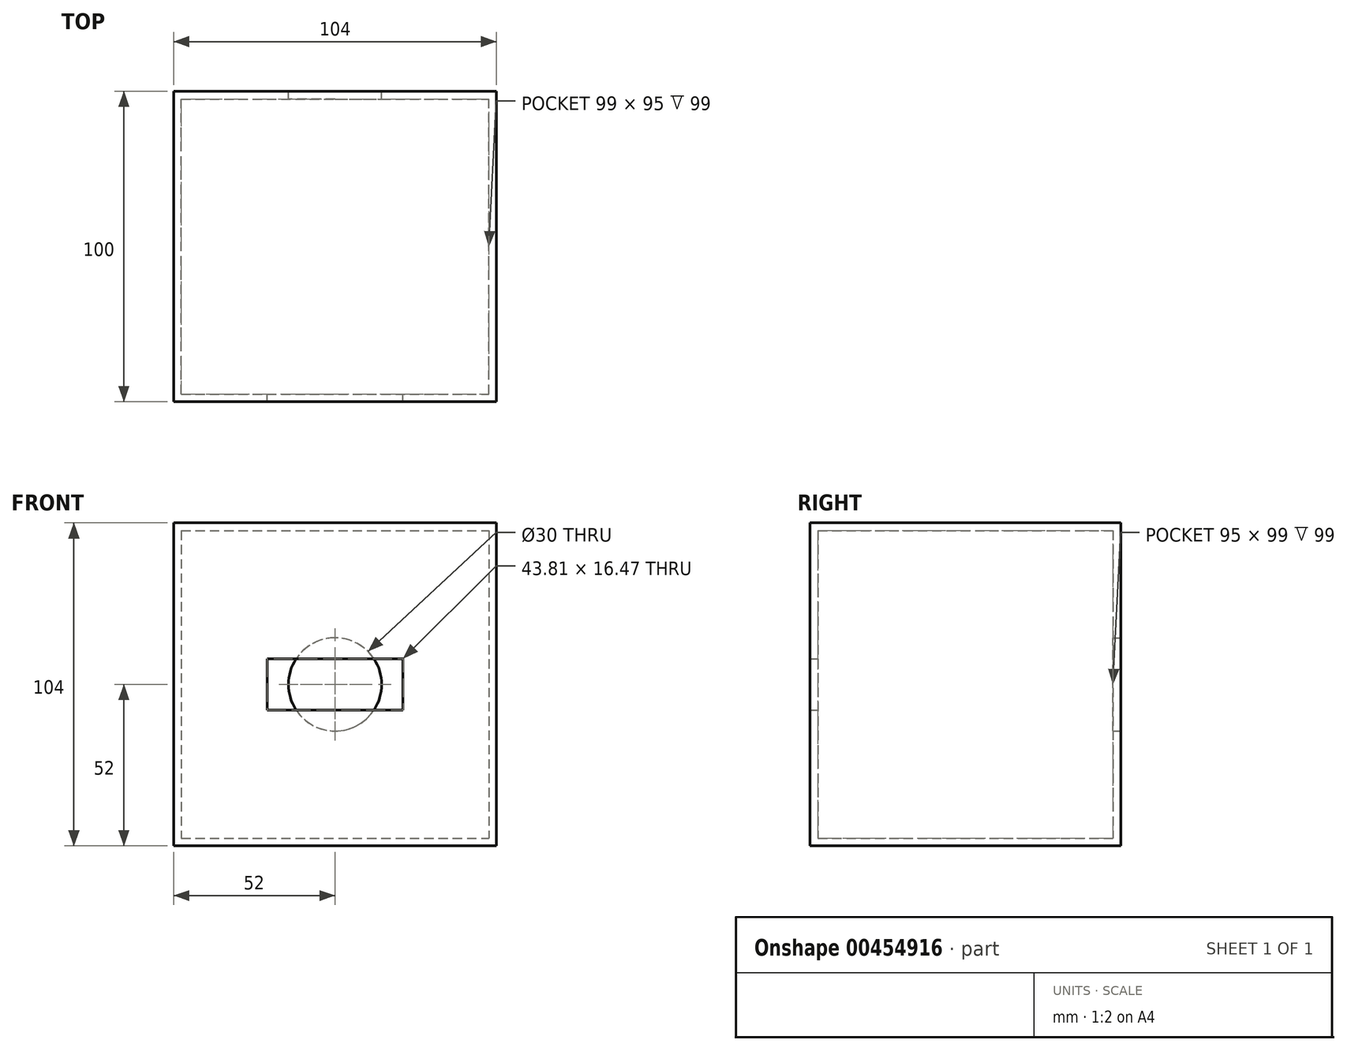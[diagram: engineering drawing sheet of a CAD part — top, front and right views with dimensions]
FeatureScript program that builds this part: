
annotation { "Feature Type Name" : "Feature", "Feature Type Description" : "" }
export const myFeature = defineFeature(function(context is Context, id is Id, definition is map)
    precondition{}
    {
        {
            var Q0;
            Q0=qCreatedBy(makeId("Front.planeOp"),FACE);
            var sketch = newSketch(context, id + "F0", { "sketchPlane" : qUnion([Q0])});
            skLineSegment(sketch, "E0.bottom", {"start": v(-52, 52) * mm, "end": v(52, 52) * mm});
            skLineSegment(sketch, "E0.top", {"start": v(-52, -52) * mm, "end": v(52, -52) * mm});
            skLineSegment(sketch, "E0.left", {"start": v(-52, 52) * mm, "end": v(-52, -52) * mm});
            skLineSegment(sketch, "E0.right", {"start": v(52, 52) * mm, "end": v(52, -52) * mm});
            skPoint(sketch, "E0.middle", {"position": v(0, 0) * mm});
            skLineSegment(sketch, "E1.bottom", {"start": v(-21.9, 8.23) * mm, "end": v(21.9, 8.23) * mm});
            skLineSegment(sketch, "E1.top", {"start": v(-21.9, -8.23) * mm, "end": v(21.9, -8.23) * mm});
            skLineSegment(sketch, "E1.left", {"start": v(-21.9, 8.23) * mm, "end": v(-21.9, -8.23) * mm});
            skLineSegment(sketch, "E1.right", {"start": v(21.9, 8.23) * mm, "end": v(21.9, -8.23) * mm});
            skSolve(sketch);
        }
        {
            var Q0;
            Q0=makeQuery(id+"F0.imprint","IMPRINT",FACE,{"disambiguationData":[TD([[makeQuery(id+"F0.imprint","IMPRINT",EDGE,{"derivedFrom":sQuery(id+"F0.wireOp",EDGE,"E0.bottom")}),-1.0]])]});
            extrude(context, id + "F1", {"entities" : qUnion([Q0]), "depth" : 100 * mm});
        }
        {
            var Q0;
            Q0=makeQuery(id+"F0.imprint","IMPRINT",FACE,{"disambiguationData":[TD([[makeQuery(id+"F0.imprint","IMPRINT",EDGE,{"derivedFrom":sQuery(id+"F0.wireOp",EDGE,"E1.bottom")}),-1.0]])]});
            extrude(context, id + "F2", {"entities" : qUnion([Q0]), "operationType" : NewBodyOperationType.ADD, "depth" : 5 * mm});
        }
        {
            var Q0;
            Q0=makeQuery(id+"F1.opExtrude","SWEPT_FACE",FACE,{"disambiguationData":[OSD([sQuery(id+"F0.wireOp",EDGE,"E1.top")])]});
            var Q1;
            Q1=makeQuery(id+"F1.opExtrude","SWEPT_FACE",FACE,{"disambiguationData":[OSD([sQuery(id+"F0.wireOp",EDGE,"E1.right")])]});
            var Q2;
            Q2=makeQuery(id+"F1.opExtrude","SWEPT_FACE",FACE,{"disambiguationData":[OSD([sQuery(id+"F0.wireOp",EDGE,"E1.bottom")])]});
            var Q3;
            Q3=makeQuery(id+"F1.opExtrude","SWEPT_FACE",FACE,{"disambiguationData":[OSD([sQuery(id+"F0.wireOp",EDGE,"E1.left")])]});
            var Q4;
            Q4=makeQuery(id+"F2.opExtrude","CAP_FACE",FACE,{"disambiguationData":[OSD([sQuery(id+"F0.wireOp",EDGE,"E1.bottom"),sQuery(id+"F0.wireOp",EDGE,"E1.top"),sQuery(id+"F0.wireOp",EDGE,"E1.left"),sQuery(id+"F0.wireOp",EDGE,"E1.right")])],"isStart":false});
            shell(context, id + "F3", {"entities" : qUnion([Q0, Q1, Q2, Q3, Q4]), "thickness" : 2.5 * mm});
        }
        {
            var Q0;
            {var subQ0=sQuery(id+"F0.wireOp",EDGE,"E1.right");var subQ1=sQuery(id+"F0.wireOp",EDGE,"E1.left");var subQ2=sQuery(id+"F0.wireOp",EDGE,"E1.top");var subQ3=sQuery(id+"F0.wireOp",EDGE,"E1.bottom");Q0=makeQuery(id+"F2.boolean.opBoolean","MERGE",FACE,{"derivedFrom":[makeQuery(id+"F1.opExtrude","CAP_FACE",FACE,{"disambiguationData":[OSD([sQuery(id+"F0.wireOp",EDGE,"E0.bottom"),sQuery(id+"F0.wireOp",EDGE,"E0.top"),sQuery(id+"F0.wireOp",EDGE,"E0.left"),sQuery(id+"F0.wireOp",EDGE,"E0.right"),subQ3,subQ2,subQ1,subQ0])],"isStart":true}),makeQuery(id+"F2.opExtrude","CAP_FACE",FACE,{"disambiguationData":[OSD([subQ3,subQ2,subQ1,subQ0])],"isStart":true})]});}
            var sketch = newSketch(context, id + "F4", { "sketchPlane" : qUnion([Q0])});
            skCircle(sketch, "E2", {"center": v(0, 0) * mm, "radius": 15 * mm});
            skSolve(sketch);
        }
        {
            var Q0;
            Q0=makeQuery(id+"F4.imprint","IMPRINT",FACE,{"disambiguationData":[TD([[makeQuery(id+"F4.imprint","IMPRINT",EDGE,{"derivedFrom":sQuery(id+"F4.wireOp",EDGE,"E2")}),1.0]])]});
            extrude(context, id + "F5", {"entities" : qUnion([Q0]), "operationType" : NewBodyOperationType.REMOVE, "oppositeDirection" : true, "depth" : 25 * mm});
        }
    });
